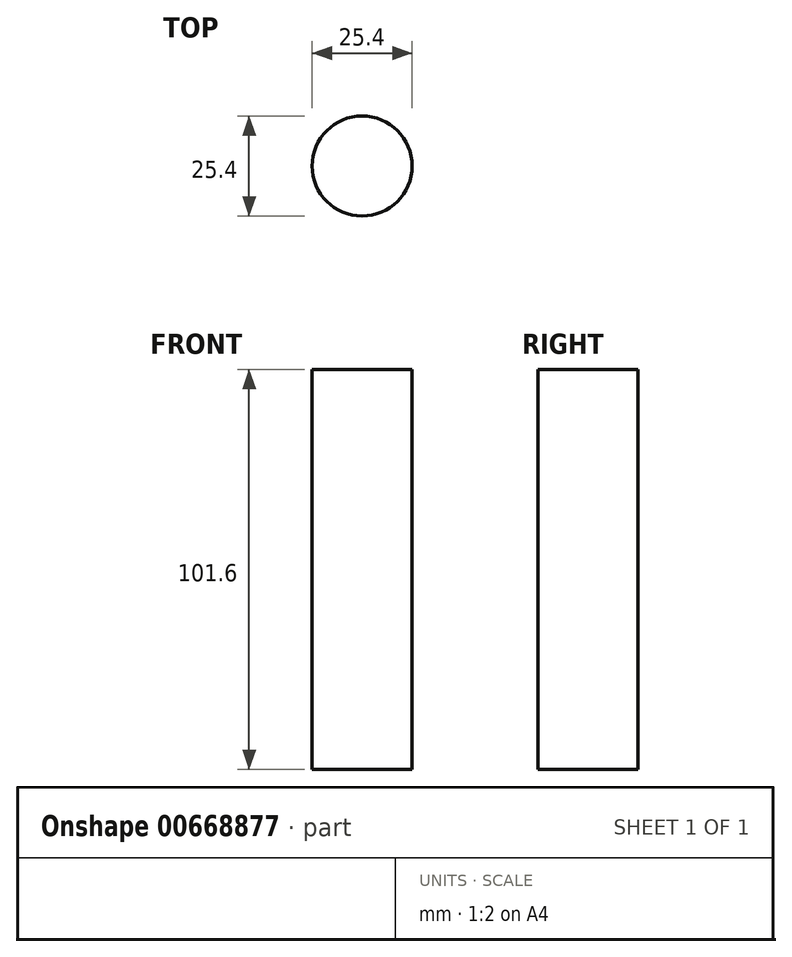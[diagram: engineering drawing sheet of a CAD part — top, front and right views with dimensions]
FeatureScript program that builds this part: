
annotation { "Feature Type Name" : "Feature", "Feature Type Description" : "" }
export const myFeature = defineFeature(function(context is Context, id is Id, definition is map)
    precondition{}
    {
        {
            var Q0;
            Q0=qCreatedBy(makeId("Top.planeOp"),FACE);
            var sketch = newSketch(context, id + "F0", { "sketchPlane" : qUnion([Q0])});
            skCircle(sketch, "E0", {"center": v(-6.96, -7.65) * mm, "radius": 12.7 * mm});
            skSolve(sketch);
        }
        {
            var Q0;
            Q0 = qSketchRegion(id + "F0", true);
            extrude(context, id + "F1", {"entities" : qUnion([Q0]), "depth" : 101.6 * mm, "offsetDistance" : 25.4 * mm});
        }
    });
